# Revit family: TELEFONO
name_source: partatom
category: Electrical Fixtures
units: mm (PartAtom-declared; Revit-internal decimal feet)

## family parameters
Always vertical = No
Cut with Voids When Loaded = No
Maintain Annotation Orientation = Yes
Part Type = Normal
Room Calculation Point = No
Round Connector Dimension = Use Diameter
Shared = Yes
Work Plane-Based = Yes

## types (1)
- TELEFONO
    A1 = 12 mm  [stored 0.0393701 ft]
    A2 = 3 mm  [stored 0.00984252 ft]
    ANCHO BASE = 37 mm
    ANCHO CONECTOR = 17 mm
    ANCHO RECEPTACULO = 36 mm  [stored 0.11811 ft]
    Default Elevation = 1219 mm
    ESPESOR = 8 mm  [stored 0.0262467 ft]
    ESPESOR BASE = 7 mm  [stored 0.0229659 ft]
    ESPESOR CONECTOR = 15 mm  [stored 0.0492126 ft]
    INCLUIR EN LISTADO = No
    LARGO BASE = 66 mm
    LARGO CONECTOR = 19 mm
    LARGO SOCKET = 22 mm  [stored 0.0721785 ft]
    LONGITUD RECEPTACULO = 65 mm  [stored 0.213255 ft]
    PROFUNDIDAD RANURA = 14 mm  [stored 0.0459318 ft]
    RADIO_1 = 1 mm  [stored 0.00328084 ft]
    RADIO_2 = 2 mm  [stored 0.00656168 ft]
    T1 = 4 mm  [stored 0.0131234 ft]
    T10 = 15 mm  [stored 0.0492126 ft]
    T11 = 4 mm  [stored 0.0131234 ft]
    T12 = 3 mm  [stored 0.00984252 ft]
    T2 = 10 mm  [stored 0.0328084 ft]
    T3 = 13 mm  [stored 0.0426509 ft]
    T4 = 6 mm  [stored 0.019685 ft]
    T5 = 7 mm  [stored 0.0229659 ft]
    T6 = 2 mm  [stored 0.00656168 ft]
    T7 = 2 mm  [stored 0.00656168 ft]
    T8 = 2 mm  [stored 0.00656168 ft]
    T9 = 4 mm  [stored 0.0131234 ft]
    X1 = 7 mm  [stored 0.0229659 ft]
    X2 = 1 mm  [stored 0.00328084 ft]
    X3 = 6 mm  [stored 0.019685 ft]

note: [stored X ft] marks values corroborated as IEEE doubles in the binary element streams (Revit-internal decimal feet)

## geometry (parser evidence)
native form markers: Sweep x8
no freeform markers — native parametric forms only
